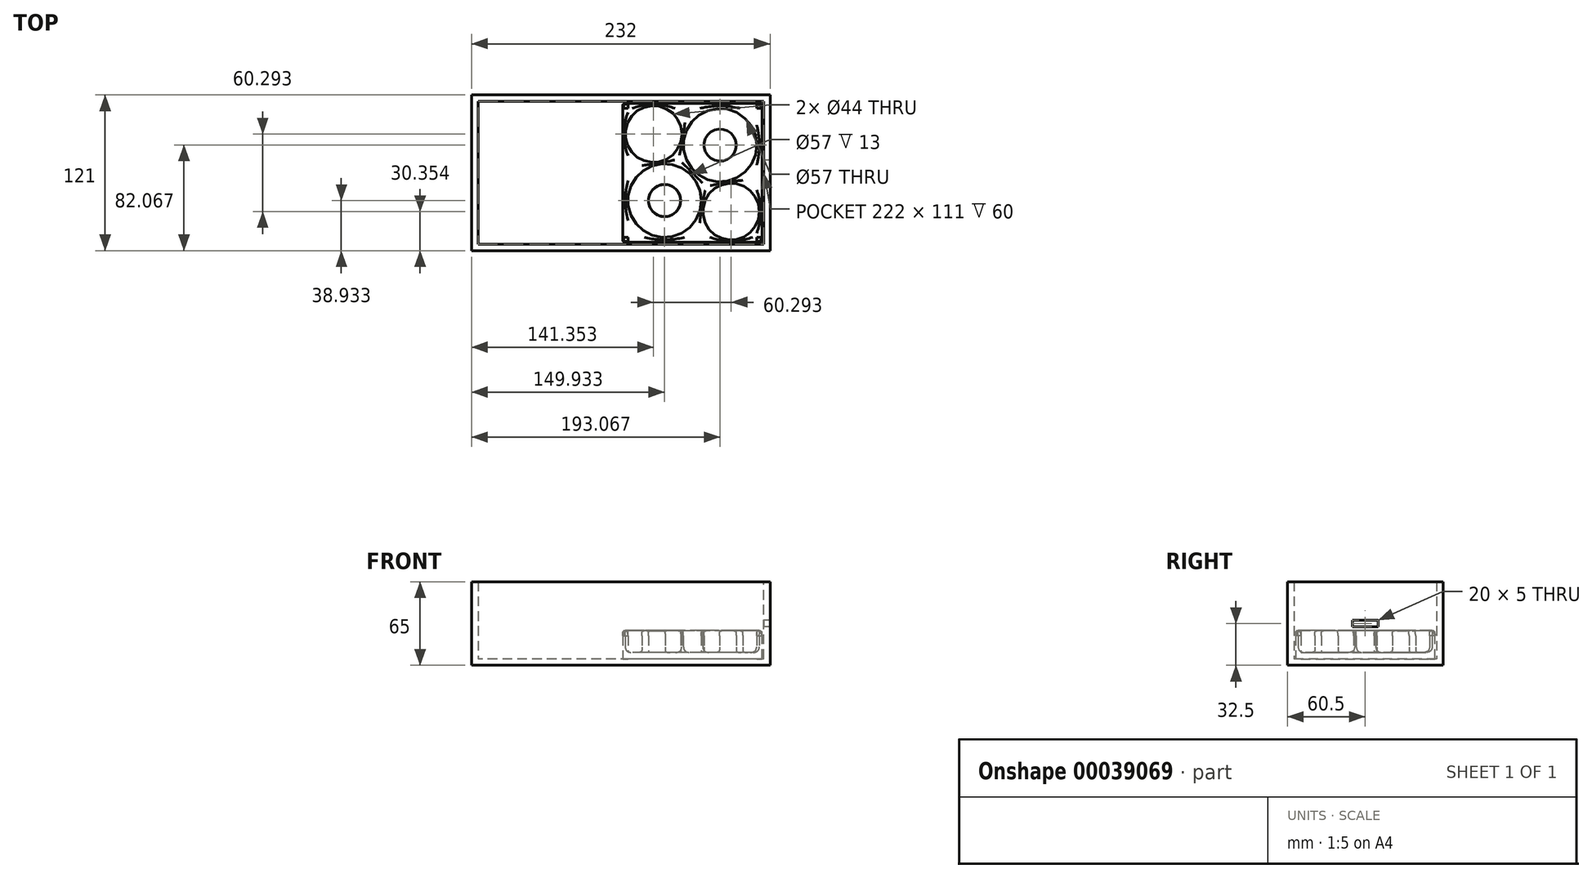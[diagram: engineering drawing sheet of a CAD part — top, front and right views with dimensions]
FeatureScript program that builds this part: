
annotation { "Feature Type Name" : "Feature", "Feature Type Description" : "" }
export const myFeature = defineFeature(function(context is Context, id is Id, definition is map)
    precondition{}
    {
        {
            var Q0;
            Q0=qCreatedBy(makeId("Top.planeOp"),FACE);
            var sketch = newSketch(context, id + "F0", { "sketchPlane" : qUnion([Q0])});
            skLineSegment(sketch, "E0.rect.bottom", {"start": v(54.07, -54.07) * mm, "end": v(-54.07, -54.07) * mm});
            skLineSegment(sketch, "E0.rect.top", {"start": v(54.07, 54.07) * mm, "end": v(-54.07, 54.07) * mm});
            skLineSegment(sketch, "E0.rect.left", {"start": v(54.07, -54.07) * mm, "end": v(54.07, 54.07) * mm});
            skLineSegment(sketch, "E0.rect.right", {"start": v(-54.07, -54.07) * mm, "end": v(-54.07, 54.07) * mm});
            skPoint(sketch, "E0.rect.middle", {"position": v(0, 0) * mm});
            skCircle(sketch, "E1", {"center": v(-21.57, -21.57) * mm, "radius": 28.5 * mm});
            skCircle(sketch, "E2", {"center": v(21.57, 21.57) * mm, "radius": 28.5 * mm});
            skCircle(sketch, "E3", {"center": v(-30.15, 30.15) * mm, "radius": 22 * mm});
            skCircle(sketch, "E4", {"center": v(30.15, -30.15) * mm, "radius": 22 * mm});
            skLineSegment(sketch, "E5", {"start": v(-54.07, -54.07) * mm, "end": v(54.07, 54.07) * mm, "construction": true});
            skLineSegment(sketch, "E6", {"start": v(-54.07, 54.07) * mm, "end": v(54.07, -54.07) * mm, "construction": true});
            skLineSegment(sketch, "E7", {"start": v(30.15, -52.15) * mm, "end": v(30.15, -54.07) * mm, "construction": true});
            skLineSegment(sketch, "E8", {"start": v(52.15, -30.15) * mm, "end": v(54.07, -30.15) * mm, "construction": true});
            skLineSegment(sketch, "E9", {"start": v(26.23, -6.55) * mm, "end": v(26.55, -8.44) * mm, "construction": true});
            skLineSegment(sketch, "E10", {"start": v(6.55, -26.23) * mm, "end": v(8.44, -26.55) * mm, "construction": true});
            skLineSegment(sketch, "E11", {"start": v(-30.15, 52.15) * mm, "end": v(-30.15, 54.07) * mm, "construction": true});
            skLineSegment(sketch, "E12", {"start": v(-52.15, 30.15) * mm, "end": v(-54.07, 30.15) * mm, "construction": true});
            skCircle(sketch, "E13", {"center": v(30.15, -30.15) * mm, "radius": 9 * mm});
            skCircle(sketch, "E14", {"center": v(-30.15, 30.15) * mm, "radius": 9 * mm});
            skCircle(sketch, "E15", {"center": v(-21.57, -21.57) * mm, "radius": 12.5 * mm});
            skCircle(sketch, "E16", {"center": v(21.57, 21.57) * mm, "radius": 12.5 * mm});
            skSolve(sketch);
        }
        {
            var Q0;
            Q0=makeQuery(id+"F0.imprint","IMPRINT",FACE,{"disambiguationData":[TD([[makeQuery(id+"F0.imprint","IMPRINT",EDGE,{"derivedFrom":sQuery(id+"F0.wireOp",EDGE,"E15")}),1.0]])]});
            var Q1;
            Q1=makeQuery(id+"F0.imprint","IMPRINT",FACE,{"disambiguationData":[TD([[makeQuery(id+"F0.imprint","IMPRINT",EDGE,{"derivedFrom":sQuery(id+"F0.wireOp",EDGE,"E1")}),1.0]])]});
            var Q2;
            Q2=makeQuery(id+"F0.imprint","IMPRINT",FACE,{"disambiguationData":[TD([[makeQuery(id+"F0.imprint","IMPRINT",EDGE,{"derivedFrom":sQuery(id+"F0.wireOp",EDGE,"E16")}),1.0]])]});
            var Q3;
            Q3=makeQuery(id+"F0.imprint","IMPRINT",FACE,{"disambiguationData":[TD([[makeQuery(id+"F0.imprint","IMPRINT",EDGE,{"derivedFrom":sQuery(id+"F0.wireOp",EDGE,"E14")}),1.0]])]});
            var Q4;
            Q4=makeQuery(id+"F0.imprint","IMPRINT",FACE,{"disambiguationData":[TD([[makeQuery(id+"F0.imprint","IMPRINT",EDGE,{"derivedFrom":sQuery(id+"F0.wireOp",EDGE,"E3")}),1.0]])]});
            var Q5;
            Q5=makeQuery(id+"F0.imprint","IMPRINT",FACE,{"disambiguationData":[TD([[makeQuery(id+"F0.imprint","IMPRINT",EDGE,{"derivedFrom":sQuery(id+"F0.wireOp",EDGE,"E2")}),1.0]])]});
            var Q6;
            Q6=makeQuery(id+"F0.imprint","IMPRINT",FACE,{"disambiguationData":[TD([[makeQuery(id+"F0.imprint","IMPRINT",EDGE,{"derivedFrom":sQuery(id+"F0.wireOp",EDGE,"E4")}),1.0]])]});
            var Q7;
            Q7=makeQuery(id+"F0.imprint","IMPRINT",FACE,{"disambiguationData":[TD([[makeQuery(id+"F0.imprint","IMPRINT",EDGE,{"derivedFrom":sQuery(id+"F0.wireOp",EDGE,"E13")}),1.0]])]});
            var Q8;
            Q8=makeQuery(id+"F0.imprint","IMPRINT",FACE,{"disambiguationData":[TD([[makeQuery(id+"F0.imprint","IMPRINT",EDGE,{"derivedFrom":sQuery(id+"F0.wireOp",EDGE,"E0.rect.bottom")}),-1.0]])]});
            extrude(context, id + "F1", {"entities" : qUnion([Q0, Q1, Q2, Q3, Q4, Q5, Q6, Q7, Q8]), "oppositeDirection" : true, "depth" : 5 * mm});
        }
        {
            var Q0;
            Q0=makeQuery(id+"F0.imprint","IMPRINT",FACE,{"disambiguationData":[TD([[makeQuery(id+"F0.imprint","IMPRINT",EDGE,{"derivedFrom":sQuery(id+"F0.wireOp",EDGE,"E0.rect.bottom")}),-1.0]])]});
            var Q1;
            Q1=makeQuery(id+"F0.imprint","IMPRINT",FACE,{"disambiguationData":[TD([[makeQuery(id+"F0.imprint","IMPRINT",EDGE,{"derivedFrom":sQuery(id+"F0.wireOp",EDGE,"E15")}),1.0]])]});
            var Q2;
            Q2=makeQuery(id+"F0.imprint","IMPRINT",FACE,{"disambiguationData":[TD([[makeQuery(id+"F0.imprint","IMPRINT",EDGE,{"derivedFrom":sQuery(id+"F0.wireOp",EDGE,"E13")}),1.0]])]});
            var Q3;
            Q3=makeQuery(id+"F0.imprint","IMPRINT",FACE,{"disambiguationData":[TD([[makeQuery(id+"F0.imprint","IMPRINT",EDGE,{"derivedFrom":sQuery(id+"F0.wireOp",EDGE,"E16")}),1.0]])]});
            var Q4;
            Q4=makeQuery(id+"F0.imprint","IMPRINT",FACE,{"disambiguationData":[TD([[makeQuery(id+"F0.imprint","IMPRINT",EDGE,{"derivedFrom":sQuery(id+"F0.wireOp",EDGE,"E14")}),1.0]])]});
            extrude(context, id + "F2", {"entities" : qUnion([Q0, Q1, Q2, Q3, Q4]), "operationType" : NewBodyOperationType.ADD, "depth" : 17 * mm});
        }
        {
            var Q0;
            {var subQ0=sQuery(id+"F0.wireOp",EDGE,"E0.rect.top");var subQ1=sQuery(id+"F0.wireOp",EDGE,"E0.rect.left");Q0=makeQuery(id+"F2.boolean.opBoolean","MERGE",EDGE,{"derivedFrom":[makeQuery(id+"F1.opExtrude","SWEPT_EDGE",EDGE,{"disambiguationData":[OSD([subQ0,subQ1])]}),makeQuery(id+"F2.opExtrude","SWEPT_EDGE",EDGE,{"disambiguationData":[OSD([subQ0,subQ1])]})]});}
            var Q1;
            {var subQ0=sQuery(id+"F0.wireOp",EDGE,"E0.rect.top");var subQ1=sQuery(id+"F0.wireOp",EDGE,"E0.rect.right");Q1=makeQuery(id+"F2.boolean.opBoolean","MERGE",EDGE,{"derivedFrom":[makeQuery(id+"F1.opExtrude","SWEPT_EDGE",EDGE,{"disambiguationData":[OSD([subQ0,subQ1])]}),makeQuery(id+"F2.opExtrude","SWEPT_EDGE",EDGE,{"disambiguationData":[OSD([subQ0,subQ1])]})]});}
            var Q2;
            {var subQ0=sQuery(id+"F0.wireOp",EDGE,"E0.rect.bottom");var subQ1=sQuery(id+"F0.wireOp",EDGE,"E0.rect.right");Q2=makeQuery(id+"F2.boolean.opBoolean","MERGE",EDGE,{"derivedFrom":[makeQuery(id+"F1.opExtrude","SWEPT_EDGE",EDGE,{"disambiguationData":[OSD([subQ0,subQ1])]}),makeQuery(id+"F2.opExtrude","SWEPT_EDGE",EDGE,{"disambiguationData":[OSD([subQ0,subQ1])]})]});}
            var Q3;
            {var subQ0=sQuery(id+"F0.wireOp",EDGE,"E0.rect.bottom");var subQ1=sQuery(id+"F0.wireOp",EDGE,"E0.rect.left");Q3=makeQuery(id+"F2.boolean.opBoolean","MERGE",EDGE,{"derivedFrom":[makeQuery(id+"F1.opExtrude","SWEPT_EDGE",EDGE,{"disambiguationData":[OSD([subQ0,subQ1])]}),makeQuery(id+"F2.opExtrude","SWEPT_EDGE",EDGE,{"disambiguationData":[OSD([subQ0,subQ1])]})]});}
            var Q4;
            Q4=makeQuery(id+"F2.opExtrude","CAP_EDGE",EDGE,{"disambiguationData":[OSD([sQuery(id+"F0.wireOp",EDGE,"E0.rect.bottom")])],"isStart":false});
            var Q5;
            Q5=makeQuery(id+"F2.opExtrude","CAP_EDGE",EDGE,{"disambiguationData":[OSD([sQuery(id+"F0.wireOp",EDGE,"E0.rect.right")])],"isStart":false});
            var Q6;
            Q6=makeQuery(id+"F2.opExtrude","CAP_EDGE",EDGE,{"disambiguationData":[OSD([sQuery(id+"F0.wireOp",EDGE,"E0.rect.top")])],"isStart":false});
            var Q7;
            Q7=makeQuery(id+"F2.opExtrude","CAP_EDGE",EDGE,{"disambiguationData":[OSD([sQuery(id+"F0.wireOp",EDGE,"E0.rect.left")])],"isStart":false});
            var Q8;
            Q8=makeQuery(id+"F2.opExtrude","CAP_EDGE",EDGE,{"disambiguationData":[OSD([sQuery(id+"F0.wireOp",EDGE,"E2")])],"isStart":false});
            var Q9;
            Q9=makeQuery(id+"F2.opExtrude","CAP_EDGE",EDGE,{"disambiguationData":[OSD([sQuery(id+"F0.wireOp",EDGE,"E4")])],"isStart":false});
            var Q10;
            Q10=makeQuery(id+"F2.opExtrude","CAP_EDGE",EDGE,{"disambiguationData":[OSD([sQuery(id+"F0.wireOp",EDGE,"E1")])],"isStart":false});
            var Q11;
            Q11=makeQuery(id+"F2.opExtrude","CAP_EDGE",EDGE,{"disambiguationData":[OSD([sQuery(id+"F0.wireOp",EDGE,"E3")])],"isStart":false});
            var Q12;
            Q12=makeQuery(id+"F2.opExtrude","CAP_EDGE",EDGE,{"disambiguationData":[OSD([sQuery(id+"F0.wireOp",EDGE,"E13")])],"isStart":false});
            var Q13;
            Q13=makeQuery(id+"F2.opExtrude","CAP_EDGE",EDGE,{"disambiguationData":[OSD([sQuery(id+"F0.wireOp",EDGE,"E14")])],"isStart":false});
            var Q14;
            Q14=makeQuery(id+"F2.opExtrude","CAP_EDGE",EDGE,{"disambiguationData":[OSD([sQuery(id+"F0.wireOp",EDGE,"E13")])],"isStart":true});
            var Q15;
            Q15=makeQuery(id+"F2.opExtrude","CAP_EDGE",EDGE,{"disambiguationData":[OSD([sQuery(id+"F0.wireOp",EDGE,"E14")])],"isStart":true});
            var Q16;
            Q16=makeQuery(id+"F2.opExtrude","CAP_EDGE",EDGE,{"disambiguationData":[OSD([sQuery(id+"F0.wireOp",EDGE,"E15")])],"isStart":false});
            var Q17;
            Q17=makeQuery(id+"F2.opExtrude","CAP_EDGE",EDGE,{"disambiguationData":[OSD([sQuery(id+"F0.wireOp",EDGE,"E15")])],"isStart":true});
            var Q18;
            Q18=makeQuery(id+"F2.opExtrude","CAP_EDGE",EDGE,{"disambiguationData":[OSD([sQuery(id+"F0.wireOp",EDGE,"E16")])],"isStart":false});
            var Q19;
            Q19=makeQuery(id+"F2.opExtrude","CAP_EDGE",EDGE,{"disambiguationData":[OSD([sQuery(id+"F0.wireOp",EDGE,"E16")])],"isStart":true});
            fillet(context, id + "F3", {"entities" : qUnion([Q0, Q1, Q2, Q3, Q4, Q5, Q6, Q7, Q8, Q9, Q10, Q11, Q12, Q13, Q14, Q15, Q16, Q17, Q18, Q19]), "radius" : 4 * mm, "tangentPropagation" : true, "rho" : 0.74, "crossSection" : FilletCrossSection.CONIC, "allowEdgeOverflow" : false});
        }
        {
            var Q0;
            Q0=makeQuery(id+"F2.opExtrude","CAP_EDGE",EDGE,{"disambiguationData":[OSD([sQuery(id+"F0.wireOp",EDGE,"E2")])],"isStart":true});
            var Q1;
            Q1=makeQuery(id+"F2.opExtrude","CAP_EDGE",EDGE,{"disambiguationData":[OSD([sQuery(id+"F0.wireOp",EDGE,"E4")])],"isStart":true});
            var Q2;
            Q2=makeQuery(id+"F2.opExtrude","CAP_EDGE",EDGE,{"disambiguationData":[OSD([sQuery(id+"F0.wireOp",EDGE,"E1")])],"isStart":true});
            var Q3;
            Q3=makeQuery(id+"F2.opExtrude","CAP_EDGE",EDGE,{"disambiguationData":[OSD([sQuery(id+"F0.wireOp",EDGE,"E3")])],"isStart":true});
            fillet(context, id + "F4", {"entities" : qUnion([Q0, Q1, Q2, Q3]), "radius" : 5 * mm, "tangentPropagation" : true, "rho" : 0.5, "crossSection" : FilletCrossSection.CONIC, "allowEdgeOverflow" : false});
        }
        {
            var Q0;
            Q0=makeQuery(id+"F1.opExtrude","CAP_FACE",FACE,{"disambiguationData":[OSD([sQuery(id+"F0.wireOp",EDGE,"E0.rect.bottom"),sQuery(id+"F0.wireOp",EDGE,"E0.rect.top"),sQuery(id+"F0.wireOp",EDGE,"E0.rect.left"),sQuery(id+"F0.wireOp",EDGE,"E0.rect.right")])],"isStart":false});
            var sketch = newSketch(context, id + "F5", { "sketchPlane" : qUnion([Q0])});
            skLineSegment(sketch, "E17.rect.bottom", {"start": v(55.5, -55.5) * mm, "end": v(-166.5, -55.5) * mm});
            skLineSegment(sketch, "E17.rect.top", {"start": v(55.5, 55.5) * mm, "end": v(-166.5, 55.5) * mm});
            skLineSegment(sketch, "E17.rect.left", {"start": v(55.5, -55.5) * mm, "end": v(55.5, 55.5) * mm});
            skLineSegment(sketch, "E17.rect.right", {"start": v(-166.5, -55.5) * mm, "end": v(-166.5, 55.5) * mm});
            skPoint(sketch, "E17.rect.middle", {"position": v(-55.5, 0) * mm});
            skLineSegment(sketch, "E18", {"start": v(55.5, 0) * mm, "end": v(54.07, 0) * mm, "construction": true});
            skLineSegment(sketch, "E19", {"start": v(0, -55.5) * mm, "end": v(0, -54.07) * mm, "construction": true});
            skLineSegment(sketch, "E20", {"start": v(54.07, 0) * mm, "end": v(-54.07, 0) * mm, "construction": true});
            skLineSegment(sketch, "E21", {"start": v(-54.07, 0) * mm, "end": v(-55.5, 0) * mm, "construction": true});
            skSolve(sketch);
        }
        {
            var Q0;
            Q0=makeQuery(id+"F5.imprint","IMPRINT",FACE,{"disambiguationData":[TD([[makeQuery(id+"F5.imprint","IMPRINT",EDGE,{"derivedFrom":sQuery(id+"F5.wireOp",EDGE,"E17.rect.bottom")}),-1.0]])]});
            var Q1;
            {var subQ2=sQuery(id+"F0.wireOp",EDGE,"E0.rect.bottom");Q1=makeQuery(id+"F5.imprint","IMPRINT",FACE,{"disambiguationData":[TD([[makeQuery(id+"F5.imprint","IMPRINT",EDGE,{"derivedFrom":makeQuery(id+"F1.opExtrude","CAP_EDGE",EDGE,{"disambiguationData":[OSD([subQ2])],"isStart":false})}),1.0]])]});}
            extrude(context, id + "F6", {"entities" : qUnion([Q0, Q1]), "depth" : 5 * mm});
        }
        {
            var Q0;
            Q0=makeQuery(id+"F6.opExtrude","SWEPT_FACE",FACE,{"disambiguationData":[OSD([sQuery(id+"F5.wireOp",EDGE,"E17.rect.top")])]});
            var sketch = newSketch(context, id + "F7", { "sketchPlane" : qUnion([Q0])});
            skPoint(sketch, "E22.top.end.orphan", {"position": v(-166.5, 19.08) * mm});
            skLineSegment(sketch, "E23.bottom", {"start": v(55.5, -10) * mm, "end": v(-171.5, -10) * mm});
            skLineSegment(sketch, "E23.top", {"start": v(55.5, 55) * mm, "end": v(-171.5, 55) * mm});
            skLineSegment(sketch, "E23.left", {"start": v(55.5, -10) * mm, "end": v(55.5, 55) * mm});
            skLineSegment(sketch, "E23.right", {"start": v(-171.5, -10) * mm, "end": v(-171.5, 55) * mm});
            skSolve(sketch);
        }
        {
            var Q0;
            {var subQ5=sQuery(id+"F7.wireOp",EDGE,"E23.top");Q0=makeQuery(id+"F7.imprint","IMPRINT",FACE,{"disambiguationData":[TD([[makeQuery(id+"F7.imprint","IMPRINT",EDGE,{"derivedFrom":subQ5}),1.0]])]});}
            var Q1;
            {var subQ0=sQuery(id+"F5.wireOp",EDGE,"E17.rect.top");var subQ1=makeQuery(id+"F6.opExtrude","CAP_EDGE",EDGE,{"disambiguationData":[OSD([subQ0])],"isStart":true});Q1=makeQuery(id+"F7.imprint","IMPRINT",FACE,{"disambiguationData":[TD([[makeQuery(id+"F7.imprint","IMPRINT",EDGE,{"derivedFrom":subQ1}),1.0]])]});}
            extrude(context, id + "F8", {"entities" : qUnion([Q0, Q1]), "operationType" : NewBodyOperationType.ADD, "depth" : 5 * mm});
        }
        {
            var Q0;
            Q0=makeQuery(id+"F8.opExtrude","CAP_FACE",FACE,{"disambiguationData":[OSD([sQuery(id+"F7.wireOp",EDGE,"E23.bottom"),sQuery(id+"F7.wireOp",EDGE,"E23.top"),sQuery(id+"F7.wireOp",EDGE,"E23.left"),sQuery(id+"F7.wireOp",EDGE,"E23.right")])],"isStart":true});
            var sketch = newSketch(context, id + "F9", { "sketchPlane" : qUnion([Q0])});
            skLineSegment(sketch, "E24.bottom", {"start": v(171.5, 55) * mm, "end": v(166.5, 55) * mm});
            skLineSegment(sketch, "E24.top", {"start": v(171.5, -10) * mm, "end": v(166.5, -10) * mm});
            skLineSegment(sketch, "E24.left", {"start": v(171.5, 55) * mm, "end": v(171.5, -10) * mm});
            skLineSegment(sketch, "E24.right", {"start": v(166.5, 55) * mm, "end": v(166.5, -10) * mm});
            skSolve(sketch);
        }
        {
            var Q0;
            {var subQ3=sQuery(id+"F9.wireOp",EDGE,"E24.bottom");Q0=makeQuery(id+"F9.imprint","IMPRINT",FACE,{"disambiguationData":[TD([[makeQuery(id+"F9.imprint","IMPRINT",EDGE,{"derivedFrom":subQ3}),-1.0]])]});}
            extrude(context, id + "F10", {"entities" : qUnion([Q0]), "operationType" : NewBodyOperationType.ADD, "depth" : 116 * mm});
        }
        {
            var Q0;
            Q0=makeQuery(id+"F10.opExtrude","SWEPT_FACE",FACE,{"disambiguationData":[OSD([sQuery(id+"F9.wireOp",EDGE,"E24.right")])]});
            var sketch = newSketch(context, id + "F11", { "sketchPlane" : qUnion([Q0])});
            skLineSegment(sketch, "E25.bottom", {"start": v(60.5, 55) * mm, "end": v(55.5, 55) * mm});
            skLineSegment(sketch, "E25.top", {"start": v(60.5, -10) * mm, "end": v(55.5, -10) * mm});
            skLineSegment(sketch, "E25.left", {"start": v(60.5, 55) * mm, "end": v(60.5, -10) * mm});
            skLineSegment(sketch, "E25.right", {"start": v(55.5, 55) * mm, "end": v(55.5, -10) * mm});
            skSolve(sketch);
        }
        {
            var Q0;
            {var subQ3=sQuery(id+"F11.wireOp",EDGE,"E25.bottom");Q0=makeQuery(id+"F11.imprint","IMPRINT",FACE,{"disambiguationData":[TD([[makeQuery(id+"F11.imprint","IMPRINT",EDGE,{"derivedFrom":subQ3}),1.0]])]});}
            extrude(context, id + "F12", {"entities" : qUnion([Q0]), "operationType" : NewBodyOperationType.ADD, "depth" : 227 * mm});
        }
        {
            var Q0;
            Q0=makeQuery(id+"F8.boolean.opBoolean","MERGE",FACE,{"derivedFrom":[makeQuery(id+"F6.opExtrude","SWEPT_FACE",FACE,{"disambiguationData":[OSD([sQuery(id+"F5.wireOp",EDGE,"E17.rect.left")])]}),makeQuery(id+"F8.opExtrude","SWEPT_FACE",FACE,{"disambiguationData":[OSD([sQuery(id+"F7.wireOp",EDGE,"E23.left")])]})]});
            var sketch = newSketch(context, id + "F13", { "sketchPlane" : qUnion([Q0])});
            skLineSegment(sketch, "E26.bottom", {"start": v(-60.5, -10) * mm, "end": v(55.5, -10) * mm});
            skLineSegment(sketch, "E26.top", {"start": v(-60.5, 55) * mm, "end": v(55.5, 55) * mm});
            skLineSegment(sketch, "E26.left", {"start": v(-60.5, -10) * mm, "end": v(-60.5, 55) * mm});
            skLineSegment(sketch, "E26.right", {"start": v(55.5, -10) * mm, "end": v(55.5, 55) * mm});
            skLineSegment(sketch, "E27.rect.bottom", {"start": v(10, 25) * mm, "end": v(-10, 25) * mm});
            skLineSegment(sketch, "E27.rect.top", {"start": v(10, 20) * mm, "end": v(-10, 20) * mm});
            skLineSegment(sketch, "E27.rect.left", {"start": v(10, 25) * mm, "end": v(10, 20) * mm});
            skLineSegment(sketch, "E27.rect.right", {"start": v(-10, 25) * mm, "end": v(-10, 20) * mm});
            skPoint(sketch, "E27.rect.middle", {"position": v(0, 22.5) * mm});
            skLineSegment(sketch, "E28", {"start": v(-60.5, 55) * mm, "end": v(60.5, -10) * mm, "construction": true});
            skSolve(sketch);
        }
        {
            var Q0;
            {var subQ2=sQuery(id+"F13.wireOp",EDGE,"E26.bottom");Q0=makeQuery(id+"F13.imprint","IMPRINT",FACE,{"disambiguationData":[TD([[makeQuery(id+"F13.imprint","IMPRINT",EDGE,{"derivedFrom":subQ2}),-1.0]])]});}
            var Q1;
            {var subQ1=makeQuery(id+"F6.opExtrude","CAP_EDGE",EDGE,{"disambiguationData":[OSD([sQuery(id+"F5.wireOp",EDGE,"E17.rect.left")])],"isStart":true});Q1=makeQuery(id+"F13.imprint","IMPRINT",FACE,{"disambiguationData":[TD([[makeQuery(id+"F13.imprint","IMPRINT",EDGE,{"derivedFrom":subQ1}),-1.0]])]});}
            extrude(context, id + "F14", {"entities" : qUnion([Q0, Q1]), "operationType" : NewBodyOperationType.ADD, "depth" : 5 * mm});
        }
    });
